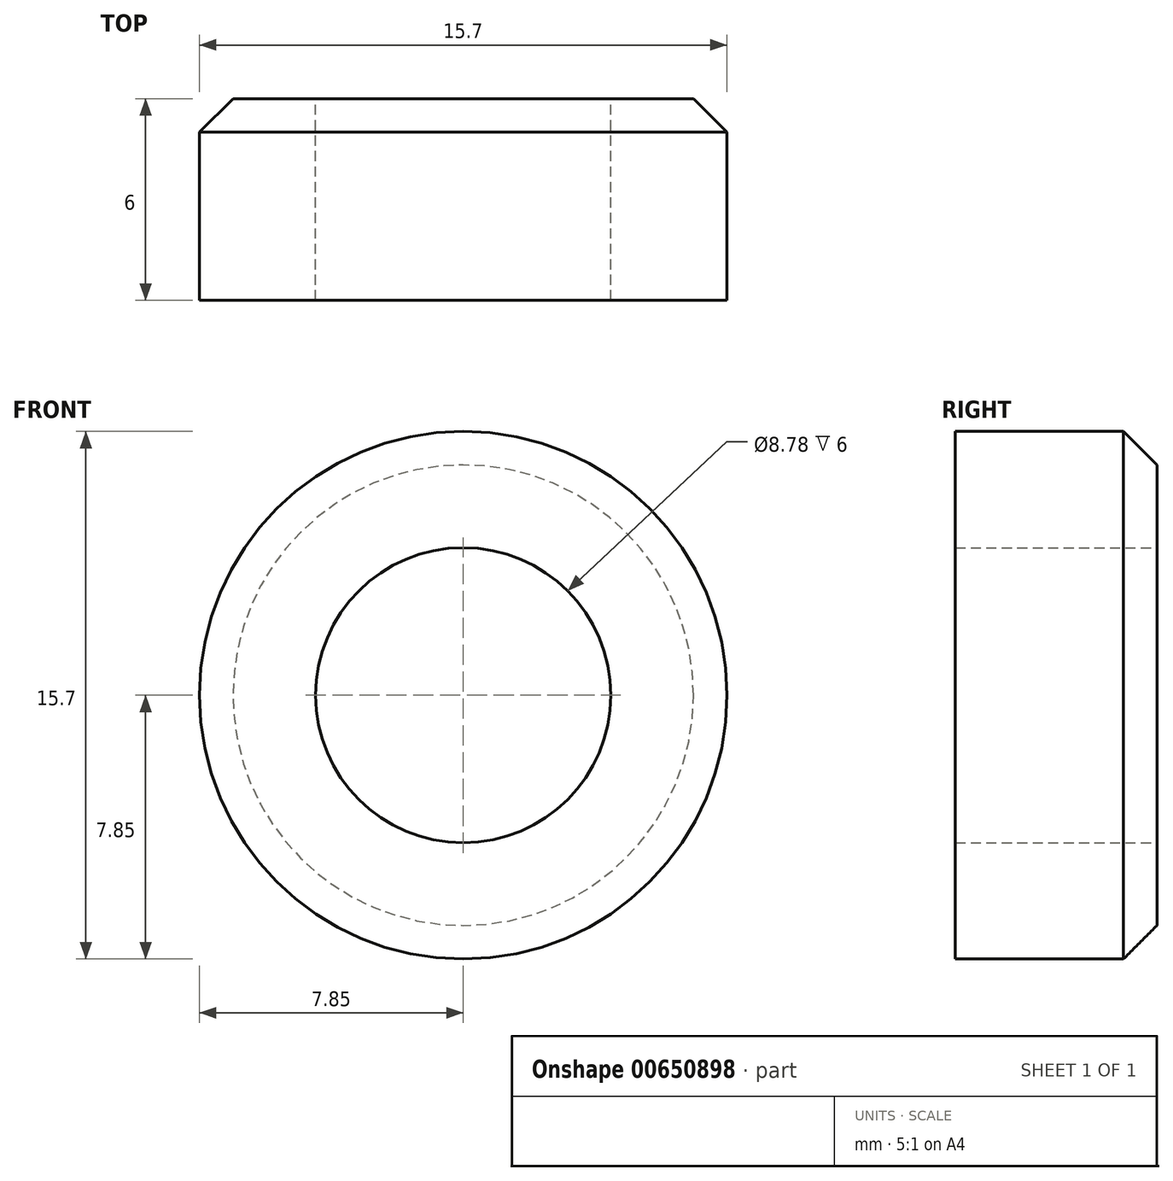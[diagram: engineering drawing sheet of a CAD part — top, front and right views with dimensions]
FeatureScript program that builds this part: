
annotation { "Feature Type Name" : "Feature", "Feature Type Description" : "" }
export const myFeature = defineFeature(function(context is Context, id is Id, definition is map)
    precondition{}
    {
        {
            var Q0;
            Q0=qCreatedBy(makeId("Front.planeOp"),FACE);
            var sketch = newSketch(context, id + "F0", { "sketchPlane" : qUnion([Q0])});
            skCircle(sketch, "E0", {"center": v(0, 0) * mm, "radius": 7.85 * mm});
            skSolve(sketch);
        }
        {
            var Q0;
            Q0=qCreatedBy(makeId("Front.planeOp"),FACE);
            var sketch = newSketch(context, id + "F1", { "sketchPlane" : qUnion([Q0])});
            skCircle(sketch, "E1", {"center": v(0, 0) * mm, "radius": 4.39 * mm});
            skSolve(sketch);
        }
        {
            var Q0;
            Q0=makeQuery(id+"F0.imprint","IMPRINT",FACE,{"disambiguationData":[TD([[makeQuery(id+"F0.imprint","IMPRINT",EDGE,{"derivedFrom":sQuery(id+"F0.wireOp",EDGE,"E0")}),1.0]])]});
            extrude(context, id + "F2", {"entities" : qUnion([Q0]), "depth" : 6 * mm, "offsetDistance" : 25 * mm});
        }
        {
            var Q0;
            Q0=sQuery(id+"F1.wireOp",VERTEX,"E1.center");
            var Q1;
            Q1=makeQuery(id+"F2.opExtrude","SWEPT_BODY",BODY,{"disambiguationData":[OSD([sQuery(id+"F0.wireOp",EDGE,"E0")])]});
            hole(context, id + "F3", {"style" : HoleStyle.SIMPLE, "endStyle" : HoleEndStyle.THROUGH, "oppositeDirection" : true, "holeDiameter" : 8.78 * mm, "majorDiameter" : 5 * mm, "isTappedThrough" : true, "tappedDepth" : 12 * mm, "tapClearance" : 3, "locations" : qUnion([Q0]), "scope" : qUnion([Q1])});
        }
        {
            var Q0;
            Q0=makeQuery(id+"F2.opExtrude","CAP_EDGE",EDGE,{"disambiguationData":[OSD([sQuery(id+"F0.wireOp",EDGE,"E0")])],"isStart":true});
            chamfer(context, id + "F4", {"entities" : qUnion([Q0]), "width" : 1 * mm, "tangentPropagation" : true});
        }
    });
